# Revit family: Smoothy 5.4
name_source: partatom
category: Lighting Fixtures
revit_build: Autodesk Revit 2017 (Build: 20160225_1515(x64)
units: mm (PartAtom-declared; Revit-internal decimal feet)

## family parameters
Cut with Voids When Loaded = Yes
Host = Face
Light Source = Yes
Part Type = Normal
Room Calculation Point = No
Round Connector Dimension = Use Diameter
Shared = No

## types (7) — shared parameters
Apparent Load = 0 VA
Apparent Load Phase 1 = 13 W
Body = L&L_Anodized aluminium
CRI = 90 (also available: CRI 80 - ref. URL Technical sheet)
Code = SY5400 I; SY5401 I
Color Filter = 16777215
Control system = -
Cutout dimensions = diam. 100 mm
Default Elevation = 1219 mm
Delivered lumen output = 800 lm (3000K, 38°, 10W, CRI 80); 645 lm (3000K, 38°, 10W, CRI 90); 1065 lm (3000K, 38°, 13W, CRI 80); 860 lm (3000K, 38°, 13W, CRI 90)
Description = recessed for outdoor applications
Dimming Lamp Color Temperature Shift = <None>
Emit from Line Length = 610 mm
Energy efficiency class = A A+ A++
Features = 16°x69° optics adjustable through 360º using the magnet provided
Geometry = Smoothy5.4_mod
Height Void = 67 mm
Height mm = 72 mm  [stored 0.23622 ft]
IP = 67
LED Colour = 3000K (also available: 2700K and 4000K - ref. URL Technical sheet)
Length mm = 109 mm  [stored 0.357612 ft]
Lens = L&L_Tempered extra-clear glass
Lumen output at source = 1115 lm (3000K, 10W, CRI 80); 900 lm (3000K, 10W, CRI 90); 1485 lm (3000K, 13W, CRI 80); 1200 lm (3000K, 13W, CRI 90)
Manufacturer = L&L Luce&Light
Material = body in anodized aluminium, trim in AISI 316L stainless steelscreen in tempered, transparent extra-clear glass (optics version) screen in sandblasted, tempered extra-clear glass (diffuse version)
Model = Smoothy 5.4
Mounting = recessed (ceiling, wall, ground)
No. and type of led = 1 high-power-density COB LED
Notes = version with 8º optics and 10W power available on request
Power = 13W (also available: 10W - ref. URL Technical sheet)
Power cables = includes 1.5 m neoprene cable H05RN-F 2x0.75/0.75 Ø6.3 mm
Power supply = 24Vdc
Power supply unit = not included
Radius Void = 50 mm  [stored 0.164042 ft]
Tilt Angle = 90.00°
Tiltable = -
Trim = L&L_Steel inox AISI 316L
URL = https://www.lucelight.it
URL Accessories and power supply units = https://www.lucelight.it
URL Catalogue = https://www.lucelight.it
URL DXF = https://www.lucelight.it
URL Description = https://www.lucelight.it
URL General code = https://www.lucelight.it
URL IES Photometric file = https://www.lucelight.it
URL Image = https://www.lucelight.it
URL Technical sheet = https://www.lucelight.it
Voltage = 24 V
Weight kg = 0.89
Width mm = 109 mm  [stored 0.357612 ft]
Wiring = -

## per-type parameters (varying)
| type | Optics | Photometric Web File |
| Smoothy 5.4_D (3000K 13W 24Vdc) | D | SMOOTHY 5.4 D [3000K 13W 24Vdc].IES |
| Smoothy 5.4_K 55° (3000K 13K 24Vdc) | 55° | SMOOTHY 5.4 K55° [3000K 13W 24Vdc].IES |
| Smoothy 5.4_L 38° (3000K 13W 24Vdc) | 38° | SMOOTHY 5.4 L 38° [3000K 13W 24Vdc].IES |
| Smoothy 5.4_M 21° (3000K 13W 24Vdc) | 21° | SMOOTHY 5.4 M 21° [3000K 13W 24Vdc].IES |
| Smoothy 5.4_P 48° (3000K 13W 24Vdc) | 48° | SMOOTHY 5.4 P (48°) [3000K 13W 24Vdc].IES |
| Smoothy 5.4_S 16° (3000K 13W 24Vdc) | 16° | SMOOTHY 5.4 S 16° [3000K 13W 24Vdc].IES |
| Smoothy 5.4_W 16°x69° (3000K 13W 24Vdc) | 16°x69° | SMOOTHY 5.4 W 16°x69° [3000K 13W 24Vdc].IES |

note: [stored X ft] marks values corroborated as IEEE doubles in the binary element streams (Revit-internal decimal feet)

## geometry (parser evidence)
native form markers: Blend x2, Sweep x8
no freeform markers — native parametric forms only
